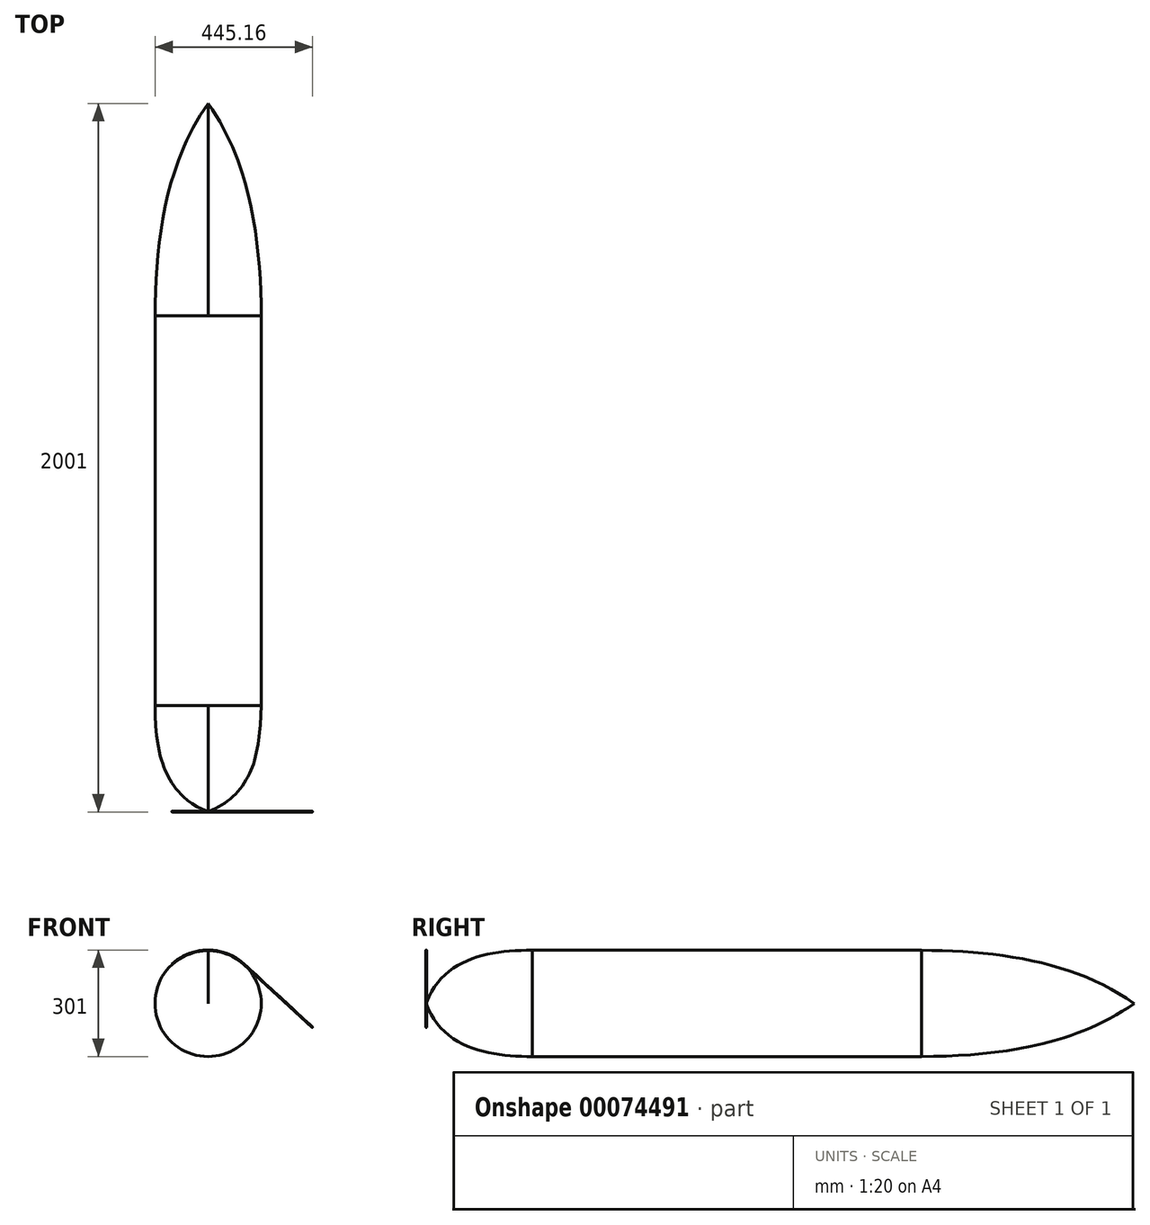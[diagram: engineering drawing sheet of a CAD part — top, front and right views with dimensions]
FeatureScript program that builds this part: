
annotation { "Feature Type Name" : "Feature", "Feature Type Description" : "" }
export const myFeature = defineFeature(function(context is Context, id is Id, definition is map)
    precondition{}
    {
        {
            var Q0;
            Q0=qCreatedBy(makeId("Right.planeOp"),FACE);
            var sketch = newSketch(context, id + "F0", { "sketchPlane" : qUnion([Q0])});
            skLineSegment(sketch, "E0", {"start": v(300, 150) * mm, "end": v(1400, 150) * mm});
            skLineSegment(sketch, "E1", {"start": v(0, 0) * mm, "end": v(2000, 0) * mm});
            skFitSpline(sketch, "E2", {"points": [v(300, 150) * mm, v(0, 0) * mm], "startDerivative": vector(-372.3, 0) * mm, "endDerivative": vector(-140.49, -383.5) * mm});
            skFitSpline(sketch, "E3", {"points": [v(1400, 150) * mm, v(2000, 0) * mm], "startDerivative": vector(674.78, 0) * mm, "endDerivative": vector(470.59, -339.57) * mm});
            skSolve(sketch);
        }
        {
            var Q0;
            Q0=makeQuery(id+"F0.imprint","IMPRINT",FACE,{"disambiguationData":[TD([[makeQuery(id+"F0.imprint","IMPRINT",EDGE,{"derivedFrom":sQuery(id+"F0.wireOp",EDGE,"E0")}),-1.0]])]});
            var Q1;
            Q1=sQuery(id+"F0.wireOp",EDGE,"E1");
            revolve(context, id + "F1", {"entities" : qUnion([Q0]), "axis" : qUnion([Q1]), "revolveType" : RevolveType.FULL});
        }
        {
            var Q0;
            Q0=qCreatedBy(makeId("Front.planeOp"),FACE);
            var sketch = newSketch(context, id + "F2", { "sketchPlane" : qUnion([Q0])});
            skCircle(sketch, "E4", {"center": v(294.49, -67.41) * mm, "radius": 38.1 * mm});
            skCircle(sketch, "E5.MirrorC", {"center": v(-294.49, -67.41) * mm, "radius": 38.1 * mm});
            skCircle(sketch, "E6.0", {"center": v(0, 0) * mm, "radius": 150 * mm, "construction": true});
            skLineSegment(sketch, "E7", {"start": v(294.49, -67.41) * mm, "end": v(101.65, 110.3) * mm});
            skLineSegment(sketch, "E8", {"start": v(294.49, -67.41) * mm, "end": v(43.54, -143.54) * mm});
            skLineSegment(sketch, "E9.MirrorCS", {"start": v(-294.49, -67.41) * mm, "end": v(-101.65, 110.3) * mm, "construction": true});
            skLineSegment(sketch, "E10.MirrorCS", {"start": v(-294.49, -67.41) * mm, "end": v(-43.54, -143.54) * mm, "construction": true});
            skArc(sketch, "E11", {"start": v(101.65, 110.3) * mm, "mid": v(0, 150) * mm, "end": v(-101.65, 110.3) * mm});
            skSolve(sketch);
        }
        {
            var Q0;
            Q0=sQuery(id+"F2.wireOp",EDGE,"E7");
            var Q1;
            Q1=sQuery(id+"F2.wireOp",VERTEX,"E7.start");
            cPlane(context, id + "F3", {"entities" : qUnion([Q0, Q1]), "cplaneType" : CPlaneType.LINE_POINT, "offset" : 150 * mm, "width" : 150 * mm, "height" : 150 * mm});
        }
        {
            var Q0;
            Q0=qCreatedBy(id+"F3.planeOp",FACE);
            var sketch = newSketch(context, id + "F4", { "sketchPlane" : qUnion([Q0])});
            skPoint(sketch, "E12.0", {"position": v(0, 150) * mm});
            skCircle(sketch, "E13", {"center": v(0, 150) * mm, "radius": 1 * mm});
            skSolve(sketch);
        }
        {
            var Q0;
            Q0=makeQuery(id+"F4.imprint","IMPRINT",FACE,{"disambiguationData":[TD([[makeQuery(id+"F4.imprint","IMPRINT",EDGE,{"derivedFrom":sQuery(id+"F4.wireOp",EDGE,"E13")}),1.0]])]});
            var Q1;
            Q1=sQuery(id+"F2.wireOp",EDGE,"E7");
            var Q2;
            Q2=sQuery(id+"F2.wireOp",EDGE,"E11");
            sweep(context, id + "F5", {"profiles" : qUnion([Q0]), "path" : qUnion([Q1, Q2])});
        }
    });
